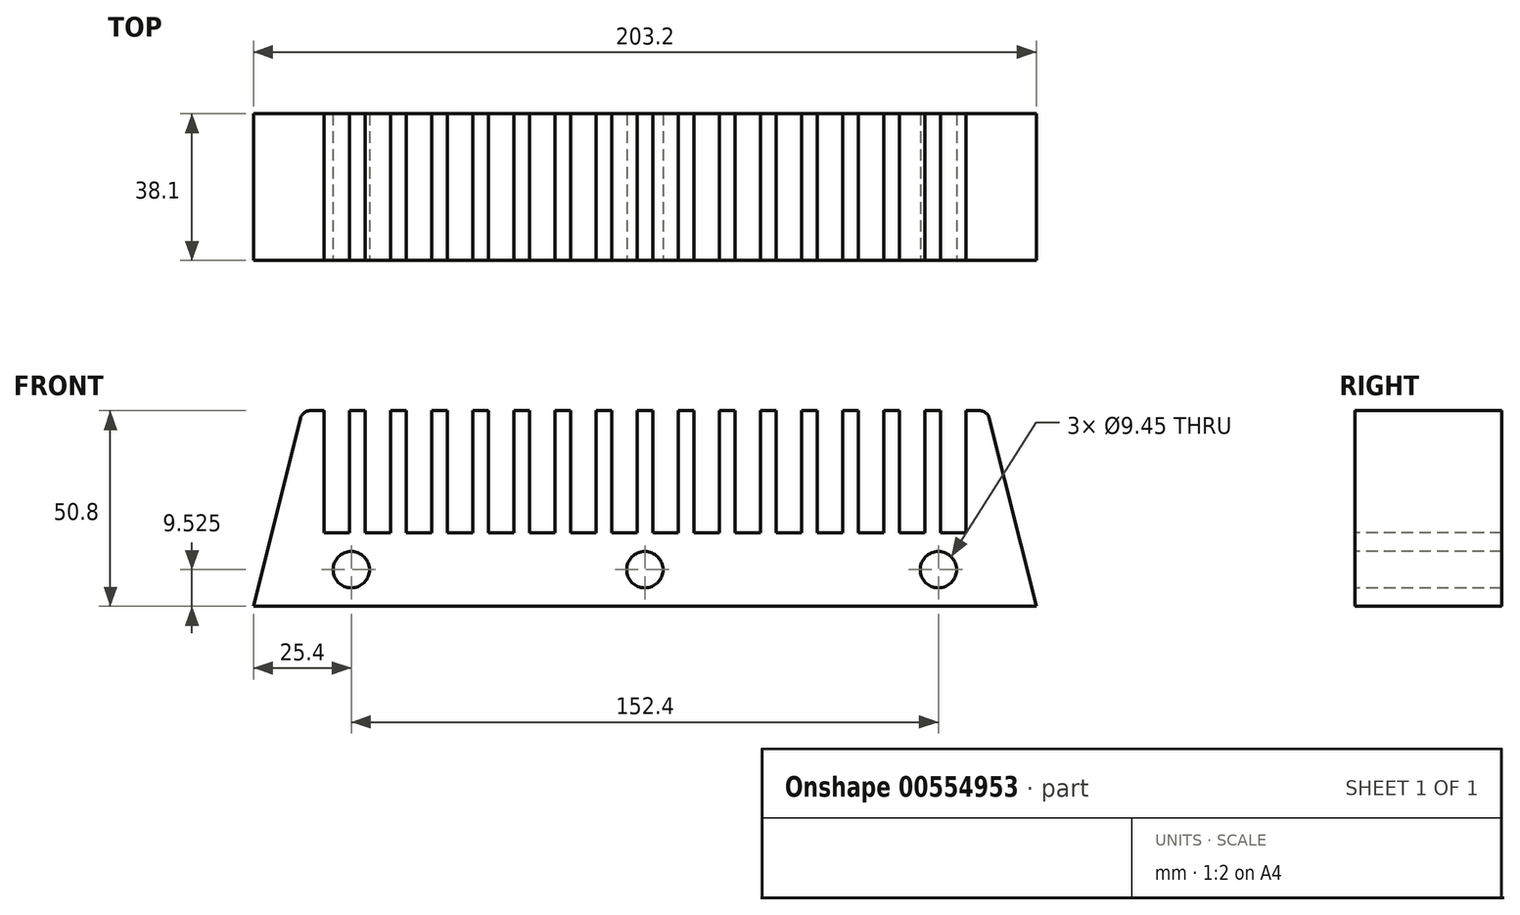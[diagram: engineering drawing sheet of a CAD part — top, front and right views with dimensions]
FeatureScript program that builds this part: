
annotation { "Feature Type Name" : "Feature", "Feature Type Description" : "" }
export const myFeature = defineFeature(function(context is Context, id is Id, definition is map)
    precondition{}
    {
        {
            var Q0;
            Q0=qCreatedBy(makeId("Front.planeOp"),FACE);
            var sketch = newSketch(context, id + "F0", { "sketchPlane" : qUnion([Q0])});
            skLineSegment(sketch, "E0", {"start": v(12.7, 50.8) * mm, "end": v(18.29, 50.8) * mm});
            skLineSegment(sketch, "E1", {"start": v(18.29, 50.8) * mm, "end": v(18.29, 19.05) * mm});
            skLineSegment(sketch, "E2", {"start": v(18.29, 19.05) * mm, "end": v(24.9, 19.05) * mm});
            skLineSegment(sketch, "E3", {"start": v(24.9, 19.05) * mm, "end": v(24.9, 50.8) * mm});
            skLineSegment(sketch, "E4", {"start": v(24.9, 50.8) * mm, "end": v(28.96, 50.8) * mm});
            skLineSegment(sketch, "E5", {"start": v(28.96, 50.8) * mm, "end": v(28.96, 19.05) * mm});
            skLineSegment(sketch, "E6", {"start": v(28.96, 19.05) * mm, "end": v(35.56, 19.05) * mm});
            skLineSegment(sketch, "E7", {"start": v(35.56, 19.05) * mm, "end": v(35.56, 50.8) * mm});
            skLineSegment(sketch, "E8", {"start": v(35.56, 50.8) * mm, "end": v(39.62, 50.8) * mm});
            skLineSegment(sketch, "E9", {"start": v(39.62, 50.8) * mm, "end": v(39.62, 19.05) * mm});
            skLineSegment(sketch, "E10", {"start": v(39.62, 19.05) * mm, "end": v(46.23, 19.05) * mm});
            skLineSegment(sketch, "E11", {"start": v(46.23, 19.05) * mm, "end": v(46.23, 50.8) * mm});
            skLineSegment(sketch, "E12", {"start": v(46.23, 50.8) * mm, "end": v(50.3, 50.8) * mm});
            skLineSegment(sketch, "E13", {"start": v(50.3, 50.8) * mm, "end": v(50.3, 19.05) * mm});
            skLineSegment(sketch, "E14", {"start": v(50.3, 19.05) * mm, "end": v(56.9, 19.05) * mm});
            skLineSegment(sketch, "E15", {"start": v(56.9, 19.05) * mm, "end": v(56.9, 50.8) * mm});
            skLineSegment(sketch, "E16", {"start": v(56.9, 50.8) * mm, "end": v(60.96, 50.8) * mm});
            skLineSegment(sketch, "E17", {"start": v(60.96, 50.8) * mm, "end": v(60.96, 19.05) * mm});
            skLineSegment(sketch, "E18", {"start": v(60.96, 19.05) * mm, "end": v(67.56, 19.05) * mm});
            skLineSegment(sketch, "E19", {"start": v(67.56, 19.05) * mm, "end": v(67.56, 50.8) * mm});
            skLineSegment(sketch, "E20", {"start": v(67.56, 50.8) * mm, "end": v(71.63, 50.8) * mm});
            skLineSegment(sketch, "E21", {"start": v(71.63, 50.8) * mm, "end": v(71.63, 19.05) * mm});
            skLineSegment(sketch, "E22", {"start": v(71.63, 19.05) * mm, "end": v(78.23, 19.05) * mm});
            skLineSegment(sketch, "E23", {"start": v(78.23, 19.05) * mm, "end": v(78.23, 50.8) * mm});
            skLineSegment(sketch, "E24", {"start": v(78.23, 50.8) * mm, "end": v(82.3, 50.8) * mm});
            skLineSegment(sketch, "E25", {"start": v(82.3, 50.8) * mm, "end": v(82.3, 19.05) * mm});
            skLineSegment(sketch, "E26", {"start": v(82.3, 19.05) * mm, "end": v(88.9, 19.05) * mm});
            skLineSegment(sketch, "E27", {"start": v(88.9, 19.05) * mm, "end": v(88.9, 50.8) * mm});
            skLineSegment(sketch, "E28", {"start": v(88.9, 50.8) * mm, "end": v(92.96, 50.8) * mm});
            skLineSegment(sketch, "E29", {"start": v(92.96, 50.8) * mm, "end": v(92.96, 19.05) * mm});
            skLineSegment(sketch, "E30", {"start": v(92.96, 19.05) * mm, "end": v(99.57, 19.05) * mm});
            skLineSegment(sketch, "E31", {"start": v(99.57, 19.05) * mm, "end": v(99.57, 50.8) * mm});
            skLineSegment(sketch, "E32", {"start": v(99.57, 50.8) * mm, "end": v(103.63, 50.8) * mm});
            skLineSegment(sketch, "E33", {"start": v(103.63, 50.8) * mm, "end": v(103.63, 19.05) * mm});
            skLineSegment(sketch, "E34", {"start": v(103.63, 19.05) * mm, "end": v(110.24, 19.05) * mm});
            skLineSegment(sketch, "E35", {"start": v(110.24, 19.05) * mm, "end": v(110.24, 50.8) * mm});
            skLineSegment(sketch, "E36", {"start": v(110.24, 50.8) * mm, "end": v(114.3, 50.8) * mm});
            skLineSegment(sketch, "E37", {"start": v(114.3, 50.8) * mm, "end": v(114.3, 19.05) * mm});
            skLineSegment(sketch, "E38", {"start": v(114.3, 19.05) * mm, "end": v(120.9, 19.05) * mm});
            skLineSegment(sketch, "E39", {"start": v(120.9, 19.05) * mm, "end": v(120.9, 50.8) * mm});
            skLineSegment(sketch, "E40", {"start": v(120.9, 50.8) * mm, "end": v(124.97, 50.8) * mm});
            skLineSegment(sketch, "E41", {"start": v(124.97, 50.8) * mm, "end": v(124.97, 19.05) * mm});
            skLineSegment(sketch, "E42", {"start": v(124.97, 19.05) * mm, "end": v(131.57, 19.05) * mm});
            skLineSegment(sketch, "E43", {"start": v(131.57, 19.05) * mm, "end": v(131.57, 50.8) * mm});
            skLineSegment(sketch, "E44", {"start": v(131.57, 50.8) * mm, "end": v(135.64, 50.8) * mm});
            skLineSegment(sketch, "E45", {"start": v(135.64, 50.8) * mm, "end": v(135.64, 19.05) * mm});
            skLineSegment(sketch, "E46", {"start": v(135.64, 19.05) * mm, "end": v(142.24, 19.05) * mm});
            skLineSegment(sketch, "E47", {"start": v(142.24, 19.05) * mm, "end": v(142.24, 50.8) * mm});
            skLineSegment(sketch, "E48", {"start": v(142.24, 50.8) * mm, "end": v(146.3, 50.8) * mm});
            skLineSegment(sketch, "E49", {"start": v(146.3, 50.8) * mm, "end": v(146.3, 19.05) * mm});
            skLineSegment(sketch, "E50", {"start": v(146.3, 19.05) * mm, "end": v(152.9, 19.05) * mm});
            skLineSegment(sketch, "E51", {"start": v(152.9, 19.05) * mm, "end": v(152.9, 50.8) * mm});
            skLineSegment(sketch, "E52", {"start": v(152.9, 50.8) * mm, "end": v(156.97, 50.8) * mm});
            skLineSegment(sketch, "E53", {"start": v(156.97, 50.8) * mm, "end": v(156.97, 19.05) * mm});
            skLineSegment(sketch, "E54", {"start": v(156.97, 19.05) * mm, "end": v(163.58, 19.05) * mm});
            skLineSegment(sketch, "E55", {"start": v(163.58, 19.05) * mm, "end": v(163.58, 50.8) * mm});
            skLineSegment(sketch, "E56", {"start": v(163.58, 50.8) * mm, "end": v(167.64, 50.8) * mm});
            skLineSegment(sketch, "E57", {"start": v(167.64, 50.8) * mm, "end": v(167.64, 19.05) * mm});
            skLineSegment(sketch, "E58", {"start": v(167.64, 19.05) * mm, "end": v(174.24, 19.05) * mm});
            skLineSegment(sketch, "E59", {"start": v(174.24, 19.05) * mm, "end": v(174.24, 50.8) * mm});
            skLineSegment(sketch, "E60", {"start": v(174.24, 50.8) * mm, "end": v(178.3, 50.8) * mm});
            skLineSegment(sketch, "E61", {"start": v(0, 0) * mm, "end": v(203.2, 0) * mm});
            skLineSegment(sketch, "E62", {"start": v(178.3, 50.8) * mm, "end": v(178.3, 19.05) * mm});
            skLineSegment(sketch, "E63", {"start": v(178.3, 19.05) * mm, "end": v(184.91, 19.05) * mm});
            skLineSegment(sketch, "E64", {"start": v(184.91, 19.05) * mm, "end": v(184.91, 50.8) * mm});
            skLineSegment(sketch, "E65", {"start": v(184.91, 50.8) * mm, "end": v(190.5, 50.8) * mm});
            skLineSegment(sketch, "E66", {"start": v(190.5, 50.8) * mm, "end": v(203.2, 0) * mm});
            skLineSegment(sketch, "E67", {"start": v(12.7, 50.8) * mm, "end": v(0, 0) * mm});
            skCircle(sketch, "E68", {"center": v(25.4, 9.53) * mm, "radius": 4.72 * mm});
            skCircle(sketch, "E69", {"center": v(101.6, 9.53) * mm, "radius": 4.72 * mm});
            skCircle(sketch, "E70", {"center": v(177.8, 9.53) * mm, "radius": 4.72 * mm});
            skPoint(sketch, "E71", {"position": v(101.6, 0) * mm});
            skLineSegment(sketch, "E72", {"start": v(101.6, 19.05) * mm, "end": v(101.6, 0) * mm, "construction": true});
            skPoint(sketch, "E73", {"position": v(101.6, 50.8) * mm});
            skSolve(sketch);
        }
        {
            var Q0;
            Q0 = qSketchRegion(id + "F0", true);
            extrude(context, id + "F1", {"entities" : qUnion([Q0]), "oppositeDirection" : true, "depth" : 38.1 * mm, "offsetDistance" : 25.4 * mm});
        }
        {
            var Q0;
            Q0=makeQuery(id+"F1.opExtrude","SWEPT_EDGE",EDGE,{"disambiguationData":[OSD([sQuery(id+"F0.wireOp",EDGE,"E65"),sQuery(id+"F0.wireOp",EDGE,"E66")])]});
            var Q1;
            Q1=makeQuery(id+"F1.opExtrude","SWEPT_EDGE",EDGE,{"disambiguationData":[OSD([sQuery(id+"F0.wireOp",EDGE,"E0"),sQuery(id+"F0.wireOp",EDGE,"E67")])]});
            fillet(context, id + "F2", {"entities" : qUnion([Q0, Q1]), "radius" : 2.54 * mm, "tangentPropagation" : true, "allowEdgeOverflow" : false});
        }
    });
